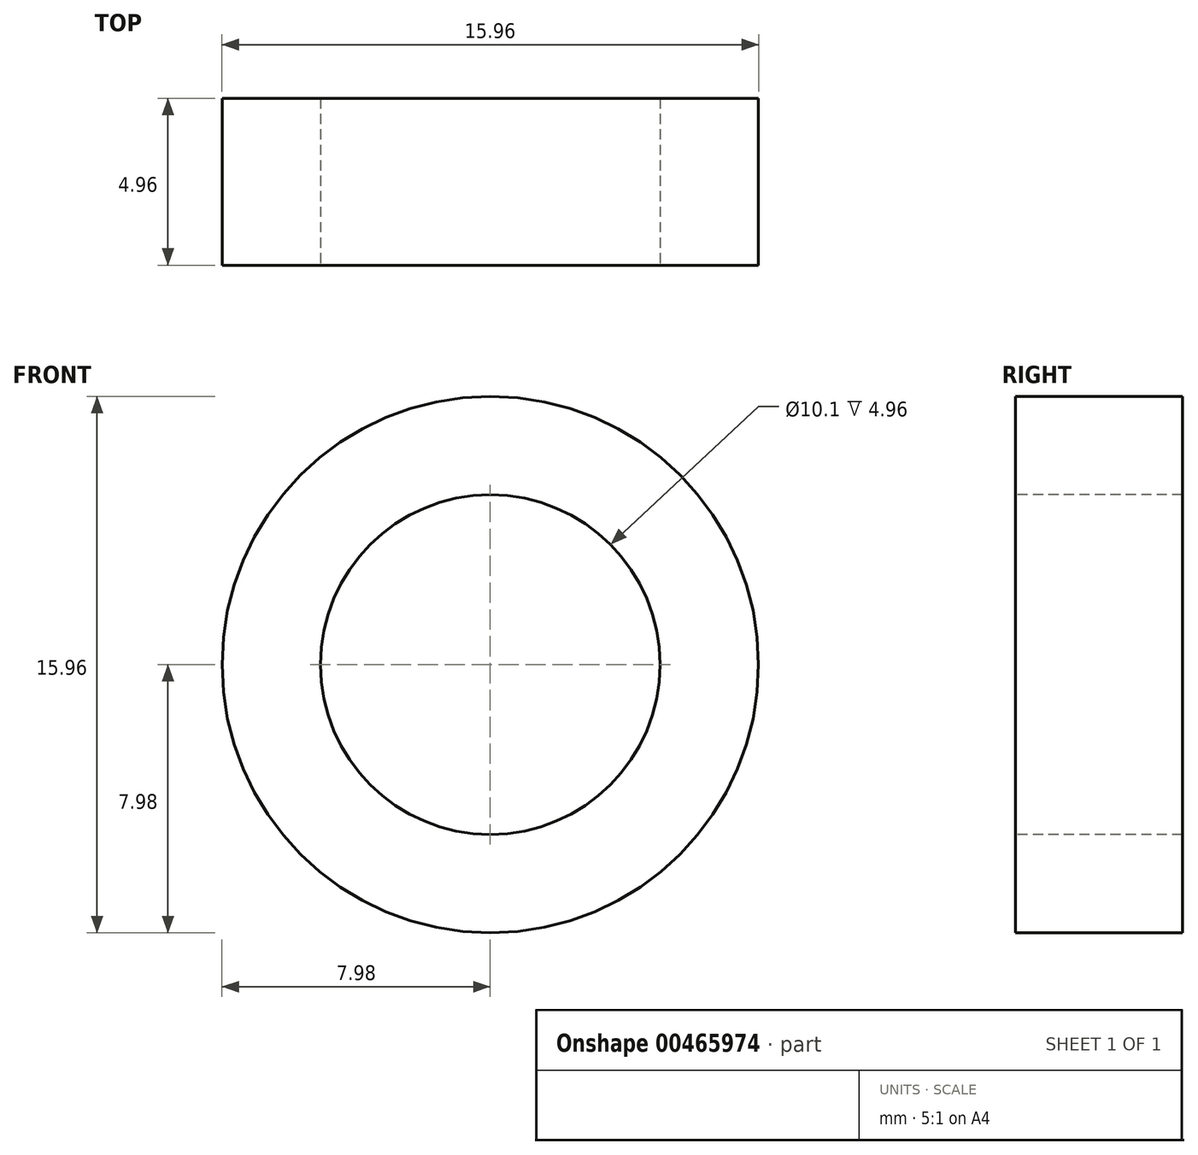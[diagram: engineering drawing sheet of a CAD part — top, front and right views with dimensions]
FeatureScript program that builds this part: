
annotation { "Feature Type Name" : "Feature", "Feature Type Description" : "" }
export const myFeature = defineFeature(function(context is Context, id is Id, definition is map)
    precondition{}
    {
        {
            var Q0;
            Q0=qCreatedBy(makeId("Right.planeOp"),FACE);
            var sketch = newSketch(context, id + "F0", { "sketchPlane" : qUnion([Q0])});
            skLineSegment(sketch, "E0", {"start": v(-2.48, 7.97) * mm, "end": v(-2.48, 5.05) * mm});
            skLineSegment(sketch, "E1", {"start": v(-2.48, 5.05) * mm, "end": v(2.48, 5.05) * mm});
            skLineSegment(sketch, "E2", {"start": v(-2.48, 7.97) * mm, "end": v(2.48, 7.97) * mm});
            skLineSegment(sketch, "E3", {"start": v(2.48, 7.97) * mm, "end": v(2.48, 5.05) * mm});
            skLineSegment(sketch, "E4", {"start": v(-4.25, 0) * mm, "end": v(4.18, 0) * mm, "construction": true});
            skSolve(sketch);
        }
        {
            var Q0;
            Q0=makeQuery(id+"F0.imprint","IMPRINT",FACE,{"disambiguationData":[TD([[makeQuery(id+"F0.imprint","IMPRINT",EDGE,{"derivedFrom":sQuery(id+"F0.wireOp",EDGE,"E0")}),1.0]])]});
            var Q1;
            Q1=sQuery(id+"F0.wireOp",EDGE,"E4");
            revolve(context, id + "F1", {"entities" : qUnion([Q0]), "axis" : qUnion([Q1]), "revolveType" : RevolveType.FULL});
        }
    });
